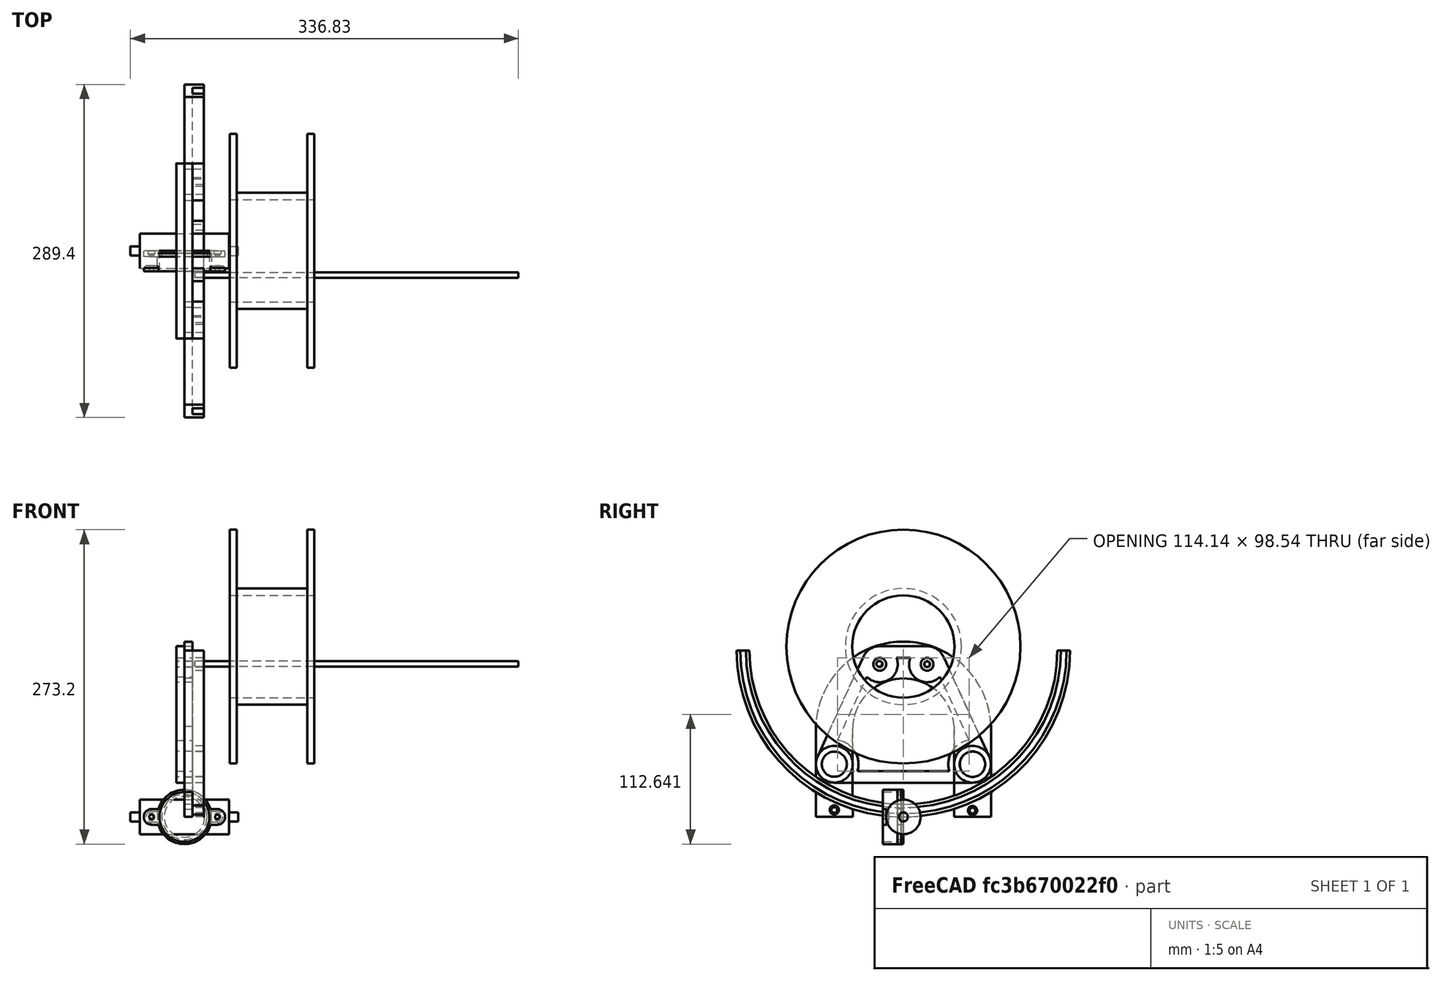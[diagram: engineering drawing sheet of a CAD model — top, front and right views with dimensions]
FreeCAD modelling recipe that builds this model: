
FCSTD DOCUMENT  (FreeCAD 1.1R39057 (Git))
Label: filament dryer new version
License: All rights reserved
objects: App::Link×17, App::FeaturePython×14, Sketcher::SketchObject×9, PartDesign::Pad×8, PartDesign::Body×7, PartDesign::Revolution×2, PartDesign::Chamfer×1, PartDesign::Hole×1, PartDesign::Fillet×1, PartDesign::SubShapeBinder×1, Assembly::JointGroup×1, Assembly::AssemblyObject×1
note: 65 computed .brp shape members not serialized (recipe doc carries the construction recipe); baked Part::Feature solids carry a one-line shape summary decoded from their .brp

FEATURE [Sketcher::SketchObject] Sketch
  ArcFitTolerance = 1e-06
  AttachmentSupport = -> [XZ_Plane]
  FullyConstrained = false
  MakeInternals = false
  MapMode = 5
  Placement = pos=(0,0,0) rot=(1,0,0;1.5708rad)
  sketch-geometry (8):
    g0: LineSegment StartX=-36.586 StartY=44.45 StartZ=0 EndX=36.586 EndY=44.45 EndZ=0
    g1: LineSegment StartX=-36.586 StartY=44.45 StartZ=0 EndX=-36.586 EndY=101.6 EndZ=0
    g2: LineSegment StartX=36.586 StartY=44.45 StartZ=0 EndX=36.586 EndY=101.6 EndZ=0
    g3: LineSegment StartX=-36.586 StartY=101.6 StartZ=0 EndX=-30.586 EndY=101.6 EndZ=0
    g4: LineSegment StartX=-30.586 StartY=101.6 StartZ=0 EndX=-30.586 EndY=50.45 EndZ=0
    g5: LineSegment StartX=30.586 StartY=101.6 StartZ=0 EndX=30.586 EndY=50.45 EndZ=0
    g6: LineSegment StartX=30.586 StartY=101.6 StartZ=0 EndX=36.586 EndY=101.6 EndZ=0
    g7: LineSegment StartX=-30.586 StartY=50.45 StartZ=0 EndX=30.586 EndY=50.45 EndZ=0
  constraints (21):
    c: Distance(g0) = 73.172
    c: Distance(g-1,g0) = 44.45
    c: Symmetric(g0,g0,g-2)
    c: Coincident(g1,g0)
    c: Vertical(g1)
    c: Coincident(g2,g0)
    c: Vertical(g2)
    c: Distance(g1,g-1) = 101.6
    c: Coincident(g3,g1)
    c: Coincident(g6,g2)
    c: Horizontal(g3)
    c: Vertical(g4)
    c: Vertical(g5)
    c: Symmetric(g5,g4,g-2)
    c: Distance(g1,g4) = 6
    c: Coincident(g3,g4)
    c: PointOnObject(g6,g5)
    c: Horizontal(g7)
    c: Distance(g0,g7) = 6
    c: Coincident(g4,g7)
    c: Coincident(g5,g7)
FEATURE [PartDesign::Revolution] Revolution
  Angle = 360
  Angle2 = 60
  Axis = (1,0,0)
  Base = (0,0,0)
  Placement = pos=(0,0,0) rot=(1,0,0;1.5708rad)
  Profile = -> Sketch
  ReferenceAxis = -> X_Axis
  Refine = true
  Reversed = true
  Suppressed = false
  Type = 0
FEATURE [PartDesign::Body] Body  label="spool filament"
  AllowCompound = false
  Group = -> [Sketch,Revolution]
  Origin = -> Origin
  Placement = pos=(76,0,148) rot=(0,0,1;0rad)
  Tip = -> Revolution
FEATURE [Sketcher::SketchObject] Sketch001
  ArcFitTolerance = 1e-06
  AttachmentSupport = -> [YZ_Plane001]
  FullyConstrained = false
  MakeInternals = false
  MapMode = 5
  Placement = pos=(0,0,0) rot=(0.57735,0.57735,0.57735;2.0944rad)
  expr: Constraints[3] = 133.7 * 2 mm
  sketch-geometry (31):
    g0: Circle CenterX=-60 CenterY=45.7733 CenterZ=0 NormalX=0 NormalY=0 NormalZ=1 AngleXU=0 Radius=11.075
    g1: Circle CenterX=60 CenterY=45.7733 CenterZ=0 NormalX=0 NormalY=0 NormalZ=1 AngleXU=0 Radius=11.075
    g2: ArcOfCircle CenterX=0 CenterY=144.7 CenterZ=0 NormalX=0 NormalY=0 NormalZ=1 AngleXU=0 Radius=133.7 StartAngle=3.14159 EndAngle=4.10707
    g3: LineSegment [constr] StartX=-133.7 StartY=144.7 StartZ=0 EndX=133.7 EndY=144.7 EndZ=0
    g4: LineSegment [constr] StartX=-133.7 StartY=144.7 StartZ=0 EndX=133.7 EndY=144.7 EndZ=0
    g5: ArcOfCircle CenterX=0 CenterY=144.7 CenterZ=0 NormalX=0 NormalY=0 NormalZ=1 AngleXU=0 Radius=144.7 StartAngle=3.14159 EndAngle=4.15941
    g6: LineSegment StartX=-133.7 StartY=144.7 StartZ=0 EndX=-144.7 EndY=144.7 EndZ=0
    g7: LineSegment StartX=133.7 StartY=144.7 StartZ=0 EndX=144.7 EndY=144.7 EndZ=0
    g8: LineSegment StartX=-76.0782 StartY=46.2231 StartZ=0 EndX=-76.0782 EndY=34.7555 EndZ=0
    g9: LineSegment StartX=76.0296 StartY=48.9403 StartZ=0 EndX=76.0296 EndY=34.7219 EndZ=0
    g10: LineSegment StartX=-76 StartY=21.5656 StartZ=0 EndX=-76 EndY=0 EndZ=0
    g11: LineSegment StartX=76 StartY=21.5656 StartZ=0 EndX=76 EndY=0 EndZ=0
    g12: LineSegment StartX=-44.0838 StartY=46.2231 StartZ=0 EndX=-44.0838 EndY=18.4768 EndZ=0
    g13: LineSegment StartX=44 StartY=48.9403 StartZ=0 EndX=44 EndY=18.4475 EndZ=0
    g14: LineSegment StartX=-44 StartY=6.85193 StartZ=0 EndX=-44 EndY=0 EndZ=0
    g15: LineSegment StartX=43.9992 StartY=6.85167 StartZ=0 EndX=43.9992 EndY=0 EndZ=0
    g16: LineSegment StartX=-76 StartY=0 StartZ=0 EndX=-44 EndY=0 EndZ=0
    g17: LineSegment StartX=43.9992 StartY=0 StartZ=0 EndX=76 EndY=0 EndZ=0
    g18: ArcOfCircle CenterX=0 CenterY=144.7 CenterZ=0 NormalX=0 NormalY=0 NormalZ=1 AngleXU=0 Radius=144.7 StartAngle=4.40342 EndAngle=5.02135
    g19: ArcOfCircle CenterX=0 CenterY=144.7 CenterZ=0 NormalX=0 NormalY=0 NormalZ=1 AngleXU=0 Radius=144.7 StartAngle=5.26537 EndAngle=6.28319
    g20: ArcOfCircle CenterX=0 CenterY=144.7 CenterZ=0 NormalX=0 NormalY=0 NormalZ=1 AngleXU=0 Radius=133.7 StartAngle=5.31726 EndAngle=6.28319
    g21: ArcOfCircle CenterX=0 CenterY=144.7 CenterZ=0 NormalX=0 NormalY=0 NormalZ=1 AngleXU=0 Radius=133.7 StartAngle=4.37638 EndAngle=5.04773
    g22: LineSegment [constr] StartX=-76.0782 StartY=46.2231 StartZ=0 EndX=-44.0838 EndY=46.2231 EndZ=0
    g23: LineSegment [constr] StartX=44 StartY=48.9403 StartZ=0 EndX=76.0296 EndY=48.9403 EndZ=0
    g24: LineSegment StartX=-76.0782 StartY=46.2231 StartZ=0 EndX=-76.0782 EndY=76.2231 EndZ=0
    g25: LineSegment StartX=76.0296 StartY=48.9403 StartZ=0 EndX=76.0296 EndY=78.9403 EndZ=0
    g26: LineSegment StartX=44 StartY=48.9403 StartZ=0 EndX=44 EndY=78.9403 EndZ=0
    g27: LineSegment StartX=-44.0838 StartY=46.2231 StartZ=0 EndX=-44.0838 EndY=76.2231 EndZ=0
    g28: LineSegment [constr] StartX=-44.0838 StartY=76.2231 StartZ=0 EndX=0 EndY=76.2231 EndZ=0
    g29: ArcOfCircle CenterX=0 CenterY=76.2231 CenterZ=0 NormalX=0 NormalY=0 NormalZ=1 AngleXU=0 Radius=44.0838 StartAngle=0.061677 EndAngle=3.14159
    g30: ArcOfCircle CenterX=0 CenterY=76.2231 CenterZ=0 NormalX=0 NormalY=0 NormalZ=1 AngleXU=0 Radius=76.0782 StartAngle=0.0357239 EndAngle=3.14159
  constraints (80):
    c: Diameter(g0) = 22.15
    c: Equal(g1,g0)
    c: Symmetric(g0,g1,g-2)
    c: Diameter(g2) = 267.4
    c: PointOnObject(g2,g-2)
    c: Horizontal(g3)
    c: PointOnObject(g2,g3)
    c: Coincident(g4,g3)
    c: Coincident(g4,g3)
    c: Coincident(g20,g3)
    c: Coincident(g2,g3)
    c: Distance(g2,g-1) = 11
    c: Coincident(g5,g2)
    c: PointOnObject(g-1,g18)
    c: Coincident(g6,g2)
    c: Horizontal(g6)
    c: Coincident(g7,g20)
    c: Horizontal(g7)
    c: Coincident(g19,g7)
    c: Coincident(g5,g6)
    c: PointOnObject(g10,g-1)
    c: Vertical(g8)
    c: PointOnObject(g11,g-1)
    c: Vertical(g9)
    c: Distance(g0,g-2) = 60
    c: PointOnObject(g9,g20)
    c: PointOnObject(g11,g19)
    c: PointOnObject(g14,g-1)
    c: Vertical(g12)
    c: PointOnObject(g15,g-1)
    c: Vertical(g13)
    c: PointOnObject(g12,g21)
    c: PointOnObject(g14,g18)
    c: Coincident(g16,g10)
    c: Coincident(g16,g14)
    c: Coincident(g17,g15)
    c: Coincident(g17,g11)
    c: Equal(g5,g18)
    c: Coincident(g5,g10)
    c: PointOnObject(g18,g14)
    c: Coincident(g5,g18)
    c: Equal(g18,g19)
    c: Coincident(g18,g15)
    c: PointOnObject(g19,g11)
    c: Coincident(g18,g19)
    c: Equal(g2,g20)
    c: Coincident(g21,g13)
    c: PointOnObject(g20,g9)
    c: Coincident(g2,g20)
    c: Equal(g2,g21)
    c: Coincident(g2,g8)
    c: PointOnObject(g21,g12)
    c: Coincident(g2,g21)
    c: Coincident(g22,g8)
    c: Coincident(g22,g12)
    c: Horizontal(g22)
    c: Coincident(g23,g13)
    c: Coincident(g23,g9)
    c: Horizontal(g23)
    c: Distance(g24) = 30
    c: Coincident(g24,g8)
    c: Vertical(g24)
    c: Coincident(g25,g9)
    c: Vertical(g25)
    c: Coincident(g26,g13)
    c: Vertical(g26)
    c: Coincident(g27,g12)
    c: Vertical(g27)
    c: Equal(g24,g27)
    c: Equal(g27,g26)
    c: Equal(g26,g25)
    c: Coincident(g28,g27)
    c: PointOnObject(g28,g-2)
    c: Horizontal(g28)
    c: Coincident(g29,g28)
    c: Coincident(g29,g27)
    c: Coincident(g29,g26)
    c: Coincident(g30,g28)
    c: Coincident(g30,g24)
    c: Coincident(g30,g25)
FEATURE [PartDesign::Pad] Pad
  Direction = (1,0,0)
  Length = 7
  Length2 = 10
  Placement = pos=(0,0,0) rot=(1,1,1;2.0944rad)
  Profile = -> Sketch001
  ReferenceAxis = -> Sketch001 [N_Axis]
  Refine = true
  Suppressed = false
  Type = 0
FEATURE [Sketcher::SketchObject] Sketch002
  ArcFitTolerance = 1e-06
  AttachmentSupport = -> [Pad]
  ExternalGeometry = -> [Pad]
  FullyConstrained = false
  MakeInternals = false
  MapMode = 5
  Placement = pos=(7,0,0) rot=(0.57735,0.57735,0.57735;2.0944rad)
  sketch-geometry (24):
    g0: ArcOfCircle CenterX=2.39e-14 CenterY=144.7 CenterZ=0 NormalX=0 NormalY=0 NormalZ=1 AngleXU=0 Radius=133.7 StartAngle=3.14159 EndAngle=6.28319
    g1: ArcOfCircle CenterX=2.39e-14 CenterY=144.7 CenterZ=0 NormalX=0 NormalY=0 NormalZ=1 AngleXU=0 Radius=144.7 StartAngle=3.14159 EndAngle=6.28319
    g2: ArcOfCircle CenterX=2.39e-14 CenterY=144.7 CenterZ=0 NormalX=0 NormalY=0 NormalZ=1 AngleXU=0 Radius=141.7 StartAngle=3.14159 EndAngle=6.28319
    g3: ArcOfCircle CenterX=2.39e-14 CenterY=144.7 CenterZ=0 NormalX=0 NormalY=0 NormalZ=1 AngleXU=0 Radius=136.7 StartAngle=3.14159 EndAngle=6.28319
    g4: LineSegment StartX=133.7 StartY=144.7 StartZ=0 EndX=136.7 EndY=144.7 EndZ=0
    g5: LineSegment StartX=141.7 StartY=144.7 StartZ=0 EndX=144.7 EndY=144.7 EndZ=0
    g6: LineSegment StartX=-136.7 StartY=144.7 StartZ=0 EndX=-133.7 EndY=144.7 EndZ=0
    g7: LineSegment StartX=-144.7 StartY=144.7 StartZ=0 EndX=-141.7 EndY=144.7 EndZ=0
    g8: Circle CenterX=-60 CenterY=6 CenterZ=0 NormalX=0 NormalY=0 NormalZ=1 AngleXU=0 Radius=2.5
    g9: Circle CenterX=-60 CenterY=6 CenterZ=0 NormalX=0 NormalY=0 NormalZ=1 AngleXU=0 Radius=4
    g10: LineSegment [constr] StartX=-60 StartY=10.7501 StartZ=0 EndX=-60 EndY=-7.18174 EndZ=0
    g11: Circle CenterX=60 CenterY=5.5 CenterZ=0 NormalX=0 NormalY=0 NormalZ=1 AngleXU=0 Radius=2.5
    g12: Circle CenterX=60 CenterY=5.5 CenterZ=0 NormalX=0 NormalY=0 NormalZ=1 AngleXU=0 Radius=4
    g13: Circle CenterX=-60 CenterY=45.7733 CenterZ=0 NormalX=0 NormalY=0 NormalZ=1 AngleXU=0 Radius=10.901
    g14: Circle CenterX=-60 CenterY=45.7733 CenterZ=0 NormalX=0 NormalY=0 NormalZ=1 AngleXU=0 Radius=16
    g15: Circle CenterX=59.9992 CenterY=45.7733 CenterZ=0 NormalX=0 NormalY=0 NormalZ=1 AngleXU=0 Radius=16
    g16: Circle CenterX=59.9992 CenterY=45.7733 CenterZ=0 NormalX=0 NormalY=0 NormalZ=1 AngleXU=0 Radius=11.0656
    g17: LineSegment [constr] StartX=0 StartY=152.301 StartZ=0 EndX=0 EndY=120.307 EndZ=0
    g18: LineSegment [constr] StartX=0 StartY=136.304 StartZ=0 EndX=37.5871 EndY=136.304 EndZ=0
    g19: Circle CenterX=-20.575 CenterY=132.671 CenterZ=0 NormalX=0 NormalY=0 NormalZ=1 AngleXU=0 Radius=2.575
    g20: Circle CenterX=-20.575 CenterY=132.671 CenterZ=0 NormalX=0 NormalY=0 NormalZ=1 AngleXU=0 Radius=5.575
    g21: ArcOfCircle [constr] CenterX=8.5e-15 CenterY=76.2231 CenterZ=0 NormalX=0 NormalY=0 NormalZ=1 AngleXU=0 Radius=60.081 StartAngle=0.738747 EndAngle=2.47765
    g22: Circle CenterX=20.575 CenterY=132.671 CenterZ=0 NormalX=0 NormalY=0 NormalZ=1 AngleXU=0 Radius=5.575
    g23: Circle CenterX=20.575 CenterY=132.671 CenterZ=0 NormalX=0 NormalY=0 NormalZ=1 AngleXU=0 Radius=2.575
  constraints (50):
    c: Coincident(g0,g-5)
    c: Coincident(g0,g-3)
    c: Coincident(g0,g-4)
    c: Coincident(g1,g0)
    c: Coincident(g1,g-3)
    c: Coincident(g1,g-4)
    c: Coincident(g2,g0)
    c: PointOnObject(g2,g-3)
    c: PointOnObject(g2,g-4)
    c: Coincident(g3,g0)
    c: PointOnObject(g3,g-3)
    c: PointOnObject(g3,g-4)
    c: Distance(g2,g1) = 3
    c: Distance(g3,g0) = 3
    c: Coincident(g4,g0)
    c: Coincident(g4,g3)
    c: Coincident(g5,g2)
    c: Coincident(g5,g1)
    c: Coincident(g6,g3)
    c: Coincident(g6,g0)
    c: Coincident(g7,g1)
    c: Coincident(g7,g2)
    c: Coincident(g9,g8)
    c: Diameter(g8) = 5
    c: Distance(g9,g-1) = 2
    c: Symmetric(g-7,g-6,g10)
    c: PointOnObject(g8,g10)
    c: Coincident(g12,g11)
    c: Diameter(g11) = 5
    c: Diameter(g12) = 8
    c: Tangent(g13,g-8) = -1.5708
    c: Coincident(g14,g13)
    c: Coincident(g16,g15)
    c: PointOnObject(g17,g-2)
    c: PointOnObject(g17,g-2)
    c: PointOnObject(g17,g-10)
    c: PointOnObject(g17,g-11)
    c: Symmetric(g17,g17,g18)
    c: PointOnObject(g18,g17)
    c: Diameter(g19) = 5.15
    c: Coincident(g20,g19)
    c: Distance(g20,g19) = 3
    c: Coincident(g21,g-11)
    c: PointOnObject(g18,g21)
    c: PointOnObject(g19,g21)
    c: Distance(g20,g17) = 15
    c: Diameter(g23) = 5.15
    c: Coincident(g22,g23)
    c: Distance(g22,g23) = 3
    c: Equal(g9,g12)
FEATURE [PartDesign::Pad] Pad001
  BaseFeature = -> Pad
  Direction = (1,0,0)
  Length = 10
  Length2 = 10
  Placement = pos=(0,0,0) rot=(1,1,1;2.0944rad)
  Profile = -> Sketch002
  ReferenceAxis = -> Sketch002 [N_Axis]
  Refine = true
  Suppressed = false
  Type = 0
FEATURE [PartDesign::Body] Body001  label="spool holder"
  AllowCompound = false
  Group = -> [Sketch001,Pad,Sketch002,Pad001]
  Origin = -> Origin001
  Tip = -> Pad001
FEATURE [Sketcher::SketchObject] Sketch003
  ArcFitTolerance = 1e-06
  AttachmentSupport = -> [YZ_Plane002]
  FullyConstrained = false
  MakeInternals = false
  MapMode = 5
  Placement = pos=(0,0,0) rot=(0.57735,0.57735,0.57735;2.0944rad)
  sketch-geometry (2):
    g0: Circle [constr] CenterX=0 CenterY=0 CenterZ=0 NormalX=0 NormalY=0 NormalZ=1 AngleXU=0 Radius=0
    g1: Circle CenterX=0 CenterY=0 CenterZ=0 NormalX=0 NormalY=0 NormalZ=1 AngleXU=0 Radius=2.5
  constraints (2):
    c: Coincident(g1,g0)
    c: Diameter(g1) = 5
FEATURE [PartDesign::Pad] Pad002
  Direction = (1,0,0)
  Length = 281
  Length2 = 10
  Placement = pos=(0,0,0) rot=(1,1,1;2.0944rad)
  Profile = -> Sketch003
  ReferenceAxis = -> Sketch003 [N_Axis]
  Refine = true
  Suppressed = false
  Type = 0
FEATURE [PartDesign::Body] Body002  label="spoon holder joins"
  AllowCompound = false
  Group = -> [Sketch003,Pad002]
  Origin = -> Origin002
  Placement = pos=(9,-21,133) rot=(0,0,1;0rad)
  Tip = -> Pad002
FEATURE [Sketcher::SketchObject] Sketch004
  ArcFitTolerance = 1e-06
  AttachmentSupport = -> [XZ_Plane003]
  FullyConstrained = true
  MakeInternals = false
  MapMode = 5
  Placement = pos=(0,0,0) rot=(1,0,0;1.5708rad)
  expr: Constraints[17] = 3.925 mm
  sketch-geometry (8):
    g0: LineSegment StartX=-46.8333 StartY=0 StartZ=0 EndX=-46.8333 EndY=3.925 EndZ=0
    g1: LineSegment StartX=-46.8333 StartY=3.925 StartZ=0 EndX=-38.8333 EndY=3.925 EndZ=0
    g2: LineSegment StartX=-38.8333 StartY=3.925 StartZ=0 EndX=-38.8333 EndY=15 EndZ=0
    g3: LineSegment StartX=-38.8333 StartY=15 StartZ=0 EndX=38.8333 EndY=15 EndZ=0
    g4: LineSegment StartX=38.8333 StartY=15 StartZ=0 EndX=38.8333 EndY=3.925 EndZ=0
    g5: LineSegment StartX=38.8333 StartY=3.925 StartZ=0 EndX=46.8333 EndY=3.925 EndZ=0
    g6: LineSegment StartX=46.8333 StartY=3.925 StartZ=0 EndX=46.8333 EndY=1.2372e-12 EndZ=0
    g7: LineSegment StartX=-46.8333 StartY=0 StartZ=0 EndX=46.8333 EndY=1.2372e-12 EndZ=0
  constraints (23):
    c: PointOnObject(g0,g-1)
    c: Vertical(g0)
    c: Coincident(g1,g0)
    c: Horizontal(g1)
    c: Coincident(g2,g1)
    c: Vertical(g2)
    c: Coincident(g3,g2)
    c: Coincident(g4,g3)
    c: Coincident(g5,g4)
    c: Horizontal(g5)
    c: Vertical(g6)
    c: Vertical(g4)
    c: Equal(g2,g4)
    c: Equal(g0,g6)
    c: Symmetric(g2,g3,g-2)
    c: Coincident(g6,g5)
    c: DistanceX(g1,g1) = 8
    c: DistanceY(g0,g0) = 3.925
    c: Distance(g2,g-1) = 15
    c: Coincident(g7,g0)
    c: Coincident(g7,g6)
    c: DistanceX(g7,g7) = 93.6666
    c: Equal(g1,g5)
FEATURE [PartDesign::Revolution] Revolution001
  Angle = 360
  Angle2 = 60
  Axis = (1,0,0)
  Base = (0,0,0)
  Placement = pos=(0,0,0) rot=(1,0,0;1.5708rad)
  Profile = -> Sketch004
  ReferenceAxis = -> X_Axis003
  Refine = true
  Suppressed = false
  Type = 0
FEATURE [PartDesign::Body] Body003  label="side bearing cilinders"
  AllowCompound = false
  Group = -> [Sketch004,Revolution001]
  Origin = -> Origin003
  Tip = -> Revolution001
FEATURE [Sketcher::SketchObject] Sketch006
  ArcFitTolerance = 1e-06
  AttachmentSupport = -> [XZ_Plane006]
  FullyConstrained = true
  MakeInternals = false
  MapMode = 5
  Placement = pos=(0,0,0) rot=(1,0,0;1.5708rad)
  sketch-geometry (3):
    g0: Circle CenterX=0 CenterY=0 CenterZ=0 NormalX=0 NormalY=0 NormalZ=1 AngleXU=0 Radius=23.6
    g1: Circle CenterX=0 CenterY=0 CenterZ=0 NormalX=0 NormalY=0 NormalZ=1 AngleXU=0 Radius=17.6
    g2: Circle CenterX=0 CenterY=0 CenterZ=0 NormalX=0 NormalY=0 NormalZ=1 AngleXU=0 Radius=21.6
  constraints (6):
    c: Diameter(g0) = 47.2
    c: Coincident(g0,g-1)
    c: Coincident(g1,g0)
    c: Distance(g1,g0) = 6
    c: Coincident(g2,g0)
    c: Distance(g2,g0) = 2
FEATURE [PartDesign::Pad] Pad004
  Direction = (0,-1,2e-16)
  Length = 17.8
  Length2 = 10
  Placement = pos=(0,0,0) rot=(1,0,0;1.5708rad)
  Profile = -> Sketch006 [Edge1,Edge3]
  ReferenceAxis = -> Sketch006 [N_Axis]
  Refine = true
  Suppressed = false
  Type = 0
FEATURE [PartDesign::Pad] Pad005
  BaseFeature = -> Pad004
  Direction = (0,-1,2e-16)
  Length = 2
  Length2 = 10
  Placement = pos=(0,0,0) rot=(1,0,0;1.5708rad)
  Profile = -> Sketch006 [Edge3,Edge2]
  ReferenceAxis = -> Sketch006 [N_Axis]
  Refine = true
  Suppressed = false
  Type = 0
FEATURE [Sketcher::SketchObject] Sketch007
  ArcFitTolerance = 1e-06
  AttachmentSupport = -> [Pad005]
  ExternalGeometry = -> [Pad005]
  FullyConstrained = true
  MakeInternals = false
  MapMode = 5
  Placement = pos=(0,-17.8,0) rot=(1,0,0;1.5708rad)
  sketch-geometry (10):
    g0: ArcOfCircle CenterX=0 CenterY=0 CenterZ=0 NormalX=0 NormalY=0 NormalZ=1 AngleXU=0 Radius=23.6 StartAngle=2.8518 EndAngle=3.43139
    g1: ArcOfCircle CenterX=-28.6 CenterY=0 CenterZ=0 NormalX=0 NormalY=0 NormalZ=1 AngleXU=0 Radius=6.74389 StartAngle=1.5708 EndAngle=4.71239
    g2: ArcOfCircle CenterX=28.6 CenterY=0 CenterZ=0 NormalX=0 NormalY=0 NormalZ=1 AngleXU=0 Radius=6.74389 StartAngle=4.71239 EndAngle=7.85398
    g3: LineSegment StartX=-28.6 StartY=6.74389 StartZ=0 EndX=-22.6159 EndY=6.74389 EndZ=0
    g4: LineSegment StartX=-28.6 StartY=-6.74389 StartZ=0 EndX=-22.6159 EndY=-6.74389 EndZ=0
    g5: LineSegment StartX=22.6159 StartY=6.74389 StartZ=0 EndX=28.6 EndY=6.74389 EndZ=0
    g6: LineSegment StartX=22.6159 StartY=-6.74389 StartZ=0 EndX=28.6 EndY=-6.74389 EndZ=0
    g7: Circle CenterX=-28.6 CenterY=0 CenterZ=0 NormalX=0 NormalY=0 NormalZ=1 AngleXU=0 Radius=1.95
    g8: Circle CenterX=28.6 CenterY=0 CenterZ=0 NormalX=0 NormalY=0 NormalZ=1 AngleXU=0 Radius=1.95
    g9: ArcOfCircle CenterX=0 CenterY=0 CenterZ=0 NormalX=0 NormalY=0 NormalZ=1 AngleXU=0 Radius=23.6 StartAngle=5.99339 EndAngle=6.57298
  constraints (28):
    c: Coincident(g0,g-1)
    c: Tangent(g0,g-3)
    c: PointOnObject(g1,g-1)
    c: Equal(g2,g1)
    c: Symmetric(g1,g2,g-2)
    c: Distance(g1,g0) = 5
    c: Coincident(g2,g5) = 1.5708
    c: Coincident(g2,g6) = -1.5708
    c: Block(g1)
    c: Block(g2)
    c: Coincident(g3,g1)
    c: Coincident(g4,g1)
    c: PointOnObject(g6,g9)
    c: Diameter(g7) = 3.9
    c: Coincident(g7,g1)
    c: Diameter(g8) = 3.9
    c: Coincident(g8,g2)
    c: Coincident(g9,g5)
    c: Coincident(g0,g3)
    c: Equal(g0,g9)
    c: Coincident(g0,g4)
    c: PointOnObject(g9,g6)
    c: Coincident(g0,g9)
    c: Horizontal(g4)
    c: Horizontal(g3)
    c: Horizontal(g5)
    c: Horizontal(g6)
    c: DistanceY(g1,g1) = 6.74389
FEATURE [PartDesign::Pad] Pad006
  BaseFeature = -> Pad005
  Direction = (0,-1,2e-16)
  Length = 5
  Length2 = 10
  Placement = pos=(0,0,0) rot=(1,0,0;1.5708rad)
  Profile = -> Sketch007
  ReferenceAxis = -> Sketch007 [N_Axis]
  Refine = true
  Reversed = true
  Suppressed = false
  Type = 0
FEATURE [PartDesign::Chamfer] Chamfer
  Angle = 45
  Base = -> Pad006 [Edge5,Edge26,Edge27,Edge25,Edge18,Edge17,Edge19]
  BaseFeature = -> Pad006
  ChamferType = 0
  FlipDirection = false
  Placement = pos=(0,0,0) rot=(1,0,0;1.5708rad)
  Refine = true
  Size = 2
  Size2 = 1
  SupportTransform = false
  Suppressed = false
  UseAllEdges = false
FEATURE [PartDesign::Body] Body005  label=" thermal and humidity sensor case 1"
  AllowCompound = false
  Group = -> [Sketch006,Pad004,Pad005,Sketch007,Pad006,Chamfer]
  Origin = -> Origin006
  Tip = -> Chamfer
FEATURE [Sketcher::SketchObject] Sketch008
  ArcFitTolerance = 1e-06
  AttachmentSupport = -> [XZ_Plane007]
  FullyConstrained = false
  MakeInternals = false
  MapMode = 5
  Placement = pos=(0,0,0) rot=(1,0,0;1.5708rad)
  expr: Constraints[7] = 6.74 * 2 mm
  sketch-geometry (11):
    g0: ArcOfCircle CenterX=0 CenterY=0 CenterZ=0 NormalX=0 NormalY=0 NormalZ=1 AngleXU=0 Radius=23.6 StartAngle=3.43122 EndAngle=5.99356
    g1: Circle CenterX=0 CenterY=0 CenterZ=0 NormalX=0 NormalY=0 NormalZ=1 AngleXU=0 Radius=19.6
    g2: ArcOfCircle CenterX=-28.6 CenterY=0 CenterZ=0 NormalX=0 NormalY=0 NormalZ=1 AngleXU=0 Radius=6.74 StartAngle=1.5708 EndAngle=4.71238
    g3: ArcOfCircle CenterX=28.6 CenterY=0 CenterZ=0 NormalX=0 NormalY=0 NormalZ=1 AngleXU=0 Radius=6.74 StartAngle=4.71239 EndAngle=7.85398
    g4: LineSegment StartX=-28.6 StartY=6.74 StartZ=0 EndX=-22.6171 EndY=6.74 EndZ=0
    g5: LineSegment StartX=-28.6 StartY=-6.74 StartZ=0 EndX=-22.6171 EndY=-6.74 EndZ=0
    g6: LineSegment StartX=22.6171 StartY=6.74 StartZ=0 EndX=28.6 EndY=6.74 EndZ=0
    g7: LineSegment StartX=22.6171 StartY=-6.74 StartZ=0 EndX=28.6 EndY=-6.74 EndZ=0
    g8: ArcOfCircle CenterX=0 CenterY=0 CenterZ=0 NormalX=0 NormalY=0 NormalZ=1 AngleXU=0 Radius=23.6 StartAngle=0.289625 EndAngle=2.85197
    g9: Circle CenterX=-28.6 CenterY=0 CenterZ=0 NormalX=0 NormalY=0 NormalZ=1 AngleXU=0 Radius=2.11661
    g10: Circle CenterX=28.6 CenterY=0 CenterZ=0 NormalX=0 NormalY=0 NormalZ=1 AngleXU=0 Radius=2.11661
  constraints (25):
    c: Diameter(g0) = 47.2
    c: Coincident(g0,g-1)
    c: Coincident(g1,g0)
    c: Distance(g1,g0) = 4
    c: PointOnObject(g2,g-1)
    c: Equal(g3,g2)
    c: Symmetric(g2,g3,g-2)
    c: Diameter(g2) = 13.48
    c: Distance(g3,g0) = 5
    c: Horizontal(g5)
    c: Coincident(g2,g4)
    c: Coincident(g3,g6) = 1.5708
    c: Coincident(g3,g7) = -1.5708
    c: Vertical(g2,g2)
    c: Coincident(g2,g5)
    c: PointOnObject(g6,g8)
    c: Coincident(g8,g4)
    c: Coincident(g0,g5)
    c: Equal(g0,g8)
    c: Coincident(g0,g7)
    c: PointOnObject(g8,g6)
    c: Coincident(g0,g8)
    c: Coincident(g9,g2)
    c: Coincident(g10,g3)
    c: Equal(g10,g9)
FEATURE [PartDesign::Pad] Pad007
  Direction = (0,-1,2e-16)
  Length = 5
  Length2 = 10
  Placement = pos=(0,0,0) rot=(1,0,0;1.5708rad)
  Profile = -> Sketch008 [Edge5,Edge4,Edge3,Edge9,Edge2,Edge1,Edge8,Edge7,Edge6]
  ReferenceAxis = -> Sketch008 [N_Axis]
  Refine = true
  Suppressed = false
  Type = 0
FEATURE [PartDesign::Hole] Hole
  BaseFeature = -> Pad007
  CustomThreadClearance = 0
  Depth = 171.97
  DepthType = 1
  Diameter = 3.9
  DrillForDepth = false
  DrillPoint = 1
  DrillPointAngle = 118
  HoleCutCountersinkAngle = 90
  HoleCutCustomValues = false
  HoleCutDepth = 2.5
  HoleCutDiameter = 6.1
  HoleCutType = 3
  ModelThread = false
  Placement = pos=(0,0,0) rot=(1,0,0;1.5708rad)
  Profile = -> Sketch008 [Edge10,Edge11]
  Refine = true
  Reversed = true
  Suppressed = false
  Tapered = false
  TaperedAngle = 90
  ThreadClass = 0
  ThreadDepth = 171.97
  ThreadDepthType = 0
  ThreadDirection = 0
  ThreadFit = 0
  ThreadSize = 0
  ThreadType = 0
  Threaded = false
  UseCustomThreadClearance = false
FEATURE [PartDesign::Fillet] Fillet
  Base = -> Hole [Edge13,Edge15,Edge14,Edge12,Edge9,Edge3,Edge6,Edge11,Edge17]
  BaseFeature = -> Hole
  Placement = pos=(0,0,0) rot=(1,0,0;1.5708rad)
  Radius = 1
  Refine = true
  SupportTransform = false
  Suppressed = false
  UseAllEdges = false
FEATURE [PartDesign::Body] Body006  label="thermal and humidity sensor case 2"
  AllowCompound = false
  Group = -> [Sketch008,Pad007,Hole,Fillet]
  Origin = -> Origin007
  Tip = -> Fillet
FEATURE [PartDesign::SubShapeBinder] Binder
  BindCopyOnChange = 0
  BindMode = 0
  ClaimChildren = false
  Context = -> Body004 [Binder.]
  Fuse = false
  MakeFace = true
  OffsetFill = false
  OffsetIntersection = false
  OffsetJoinType = 0
  OffsetOpenResult = false
  PartialLoad = false
  Refine = true
  Relative = true
  Support = -> [Body001[Pad001.Face33,Pad001.Face34]]
  _Version = 2
FEATURE [Sketcher::SketchObject] Sketch005
  ArcFitTolerance = 1e-06
  AttachmentSupport = -> [YZ_Plane004]
  ExternalGeometry = -> [Binder]
  FullyConstrained = false
  MakeInternals = false
  MapMode = 5
  Placement = pos=(0,0,0) rot=(0.57735,0.57735,0.57735;2.0944rad)
  sketch-geometry (24):
    g0: Circle CenterX=-60 CenterY=45.77 CenterZ=0 NormalX=0 NormalY=0 NormalZ=1 AngleXU=0 Radius=11
    g1: Circle CenterX=59.9999 CenterY=45.77 CenterZ=0 NormalX=0 NormalY=0 NormalZ=1 AngleXU=0 Radius=11
    g2: LineSegment [constr] StartX=-60 StartY=45.77 StartZ=0 EndX=-60 EndY=0 EndZ=0
    g3: ArcOfCircle CenterX=-60 CenterY=45.77 CenterZ=0 NormalX=0 NormalY=0 NormalZ=1 AngleXU=0 Radius=16 StartAngle=2.71191 EndAngle=4.71239
    g4: ArcOfCircle CenterX=59.9999 CenterY=45.77 CenterZ=0 NormalX=0 NormalY=0 NormalZ=1 AngleXU=0 Radius=16 StartAngle=4.71239 EndAngle=6.71287
    g5: LineSegment StartX=-39.8754 StartY=39.77 StartZ=0 EndX=39.8753 EndY=39.77 EndZ=0
    g6: ArcOfCircle CenterX=59.9999 CenterY=45.77 CenterZ=0 NormalX=0 NormalY=0 NormalZ=1 AngleXU=0 Radius=21 StartAngle=1.71073 EndAngle=3.43134
    g7: ArcOfCircle CenterX=-60 CenterY=45.77 CenterZ=0 NormalX=0 NormalY=0 NormalZ=1 AngleXU=0 Radius=21 StartAngle=5.99343 EndAngle=7.71405
    g8: GeomPoint [constr] X=0 Y=151.304 Z=0
    g9: Circle CenterX=-20.575 CenterY=132.671 CenterZ=0 NormalX=0 NormalY=0 NormalZ=1 AngleXU=0 Radius=2.575
    g10: Circle CenterX=20.575 CenterY=132.671 CenterZ=0 NormalX=0 NormalY=0 NormalZ=1 AngleXU=0 Radius=2.36628
    g11: Circle [constr] CenterX=-20.575 CenterY=132.671 CenterZ=0 NormalX=0 NormalY=0 NormalZ=1 AngleXU=0 Radius=5.63976
    g12: Circle [constr] CenterX=20.575 CenterY=132.671 CenterZ=0 NormalX=0 NormalY=0 NormalZ=1 AngleXU=0 Radius=5.575
    g13: LineSegment StartX=-74.5456 StartY=52.4353 StartZ=0 EndX=-34.7931 EndY=139.186 EndZ=0
    g14: LineSegment StartX=74.5455 StartY=52.4353 StartZ=0 EndX=34.7931 EndY=139.186 EndZ=0
    g15: ArcOfCircle CenterX=-20.575 CenterY=132.671 CenterZ=0 NormalX=0 NormalY=0 NormalZ=1 AngleXU=0 Radius=15.6398 StartAngle=3.91379 EndAngle=6.6521
    g16: ArcOfCircle CenterX=20.575 CenterY=132.671 CenterZ=0 NormalX=0 NormalY=0 NormalZ=1 AngleXU=0 Radius=15.6398 StartAngle=0.429681 EndAngle=1.5708
    g17: LineSegment StartX=-57.071 StartY=66.5647 StartZ=0 EndX=-31.779 EndY=121.759 EndZ=0
    g18: LineSegment StartX=57.071 StartY=66.5647 StartZ=0 EndX=31.779 EndY=121.759 EndZ=0
    g19: LineSegment StartX=-5.9875 StartY=138.311 StartZ=0 EndX=5.9875 EndY=138.311 EndZ=0
    g20: ArcOfCircle CenterX=-20.575 CenterY=132.671 CenterZ=0 NormalX=0 NormalY=0 NormalZ=1 AngleXU=0 Radius=15.6398 StartAngle=1.5708 EndAngle=2.71191
    g21: ArcOfCircle CenterX=20.575 CenterY=132.671 CenterZ=0 NormalX=0 NormalY=0 NormalZ=1 AngleXU=0 Radius=15.6398 StartAngle=2.77268 EndAngle=5.51099
    g22: LineSegment StartX=-20.575 StartY=148.311 StartZ=0 EndX=20.575 EndY=148.311 EndZ=0
    g23: LineSegment StartX=-60 StartY=29.77 StartZ=0 EndX=59.9999 EndY=29.77 EndZ=0
  constraints (52):
    c: Diameter(g0) = 22
    c: PointOnObject(g2,g-1)
    c: Block(g1)
    c: PointOnObject(g3,g2)
    c: Distance(g0,g3) = 5
    c: Distance(g1,g4) = 5
    c: Block(g2)
    c: Coincident(g0,g2)
    c: Coincident(g3,g0)
    c: Coincident(g4,g1)
    c: Horizontal(g5)
    c: Coincident(g6,g1)
    c: Coincident(g6,g5)
    c: Coincident(g7,g0)
    c: Coincident(g7,g5)
    c: Distance(g0,g7) = 10
    c: Distance(g6,g1) = 10
    c: PointOnObject(g8,g-2)
    c: Coincident(g9,g-5)
    c: Equal(g9,g-5)
    c: Coincident(g10,g-4)
    c: Coincident(g11,g9)
    c: Coincident(g12,g10)
    c: Tangent(g12,g-4)
    c: Coincident(g15,g9)
    c: Coincident(g16,g10)
    c: Distance(g11,g15) = 10
    c: Block(g11)
    c: Tangent(g4,g14) = -1.5708
    c: Tangent(g3,g13) = 1.5708
    c: Coincident(g17,g7)
    c: Coincident(g18,g6)
    c: Parallel(g18,g14)
    c: Parallel(g17,g13)
    c: Distance(g13,g17) = 10
    c: Distance(g14,g18) = 10
    c: Coincident(g20,g13) = 1.5708
    c: Coincident(g15,g17)
    c: Coincident(g21,g18)
    c: Tangent(g16,g14) = -1.5708
    c: PointOnObject(g19,g21)
    c: Coincident(g15,g19)
    c: Coincident(g15,g20)
    c: Equal(g16,g21)
    c: PointOnObject(g21,g19)
    c: Coincident(g16,g21)
    c: Coincident(g22,g20)
    c: Coincident(g22,g16)
    c: Horizontal(g22)
    c: Coincident(g23,g3)
    c: Tangent(g23,g4) = -1.5708
    c: Horizontal(g23)
FEATURE [PartDesign::Pad] Pad008
  Direction = (1,0,0)
  Length = 14
  Length2 = 10
  Midplane = true
  Placement = pos=(0,0,0) rot=(1,1,1;2.0944rad)
  Profile = -> Sketch005
  ReferenceAxis = -> Sketch005 [N_Axis]
  Refine = true
  Suppressed = false
  Type = 0
FEATURE [PartDesign::Body] Body004  label="spoon holder middle section"
  AllowCompound = false
  Group = -> [Sketch005,Binder,Pad008]
  Origin = -> Origin004
  Tip = -> Pad008
FEATURE [App::Link] side_bearing_cilinders  label="side bearing cilinders001"
  LinkPlacement = pos=(53.8333,-60,45.7733) rot=(1,0,0;4.71239rad)
  LinkedObject = -> Body003
  Placement = pos=(53.8333,-60,45.7733) rot=(1,0,0;4.71239rad)
FEATURE [App::Link] side_bearing_cilinders001  label="side bearing cilinders002"
  LinkPlacement = pos=(147.5,-60,45.7733) rot=(-1,0,0;1.5708rad)
  LinkedObject = -> Body003
  Placement = pos=(147.5,-60,45.7733) rot=(-1,0,0;1.5708rad)
FEATURE [App::Link] side_bearing_cilinders002  label="side bearing cilinders003"
  LinkPlacement = pos=(241.167,-60,45.7733) rot=(-1,0,0;1.5708rad)
  LinkedObject = -> Body003
  Placement = pos=(241.167,-60,45.7733) rot=(-1,0,0;1.5708rad)
FEATURE [App::Link] side_bearing_cilinders003  label="side bearing cilinders004"
  LinkPlacement = pos=(147.5,59.9999,45.7733) rot=(-1,0,0;1.5708rad)
  LinkedObject = -> Body003
  Placement = pos=(147.5,59.9999,45.7733) rot=(-1,0,0;1.5708rad)
FEATURE [App::Link] side_bearing_cilinders004  label="side bearing cilinders005"
  LinkPlacement = pos=(53.8333,59.9999,45.7733) rot=(1,0,0;4.71239rad)
  LinkedObject = -> Body003
  Placement = pos=(53.8333,59.9999,45.7733) rot=(1,0,0;4.71239rad)
FEATURE [App::Link] side_bearing_cilinders005  label="side bearing cilinders006"
  LinkPlacement = pos=(241.666,59.9992,45.7733) rot=(1,0,0;1.5708rad)
  LinkedObject = -> Body003
  Placement = pos=(241.666,59.9992,45.7733) rot=(1,0,0;1.5708rad)
FEATURE [App::Link] spoon_holder_middle_section  label="spoon holder middle section001"
  LinkPlacement = pos=(194.333,7.29e-14,0.00330997) rot=(0,0,1;0rad)
  LinkedObject = -> Body004
  Placement = pos=(194.333,7.29e-14,0.00330997) rot=(0,0,1;0rad)
FEATURE [App::Link] spoon_holder_middle_section001  label="spoon holder middle section002"
  LinkPlacement = pos=(100.667,1.3e-15,0.00330997) rot=(0,0,1;0rad)
  LinkedObject = -> Body004
  Placement = pos=(100.667,1.3e-15,0.00330997) rot=(0,0,1;0rad)
FEATURE [App::Link] spool_holder  label="spool holder001"
  LinkedObject = -> Body001
FEATURE [App::FeaturePython] GroundedJoint  # Assembly grounded joint (typed FeaturePython)
  ObjectToGround = -> spool_holder
FEATURE [App::Link] spool_holder001  label="spool holder002"
  LinkPlacement = pos=(292,-0.000813,-2.02853e-06) rot=(0,0,1;3.14159rad)
  LinkedObject = -> Body001
  Placement = pos=(292,-0.000813,-2.02853e-06) rot=(0,0,1;3.14159rad)
FEATURE [App::FeaturePython] Joint  label="Fijo"  # Assembly joint (typed FeaturePython)
  Activated = true
  AngleMax = 0
  AngleMin = 0
  Detach1 = false
  Detach2 = false
  Distance = 0
  Distance2 = 0
  EnableAngleMax = false
  EnableAngleMin = false
  EnableLengthMax = false
  EnableLengthMin = false
  JointType = 0 (Fixed)
  LengthMax = 0
  LengthMin = 0
  Placement1 = pos=(-46.8333,0,7.1e-15) rot=(0.707107,0,0.707107;3.14159rad)
  Placement2 = pos=(7,-60,45.7733) rot=(0.57735,0.57735,0.57735;2.0944rad)
  Reference1 = -> Assembly [side_bearing_cilinders.Edge1,side_bearing_cilinders.Edge1]
  Reference2 = -> Assembly [spool_holder.Edge74,spool_holder.Edge74]
FEATURE [App::FeaturePython] Joint001  label="Fijo001"  # Assembly joint (typed FeaturePython)
  Activated = true
  AngleMax = 0
  AngleMin = 0
  Detach1 = false
  Detach2 = false
  Distance = 0
  Distance2 = 0
  EnableAngleMax = false
  EnableAngleMin = false
  EnableLengthMax = false
  EnableLengthMin = false
  JointType = 0 (Fixed)
  LengthMax = 0
  LengthMin = 0
  Placement1 = pos=(46.8333,0,0) rot=(0.707107,0,0.707107;3.14159rad)
  Placement2 = pos=(-2.84e-14,-60,45.77) rot=(0.57735,0.57735,0.57735;2.0944rad)
  Reference1 = -> Assembly [side_bearing_cilinders.Edge8,side_bearing_cilinders.Edge8]
  Reference2 = -> Assembly [spoon_holder_middle_section001.Face3,spoon_holder_middle_section001.Face3]
FEATURE [App::FeaturePython] Joint002  label="Fijo002"  # Assembly joint (typed FeaturePython)
  Activated = true
  AngleMax = 0
  AngleMin = 0
  Detach1 = false
  Detach2 = false
  Distance = 0
  Distance2 = 0
  EnableAngleMax = false
  EnableAngleMin = false
  EnableLengthMax = false
  EnableLengthMin = false
  JointType = 0 (Fixed)
  LengthMax = 0
  LengthMin = 0
  Placement1 = pos=(-46.8333,0,0) rot=(-0.707107,0,-0.707107;3.14159rad)
  Placement2 = pos=(46.8333,0,0) rot=(0.707107,0,0.707107;3.14159rad)
  Reference1 = -> Assembly [side_bearing_cilinders001.Edge1,side_bearing_cilinders001.Edge1]
  Reference2 = -> Assembly [side_bearing_cilinders.Face7,side_bearing_cilinders.Face7]
FEATURE [App::FeaturePython] Joint003  label="Fijo003"  # Assembly joint (typed FeaturePython)
  Activated = true
  AngleMax = 0
  AngleMin = 0
  Detach1 = false
  Detach2 = false
  Distance = 0
  Distance2 = 0
  EnableAngleMax = false
  EnableAngleMin = false
  EnableLengthMax = false
  EnableLengthMin = false
  JointType = 0 (Fixed)
  LengthMax = 0
  LengthMin = 0
  Placement1 = pos=(46.8333,0,0) rot=(-0.707107,0,-0.707107;3.14159rad)
  Placement2 = pos=(-2.84e-14,-60,45.77) rot=(0.57735,0.57735,0.57735;2.0944rad)
  Reference1 = -> Assembly [side_bearing_cilinders001.Edge8,side_bearing_cilinders001.Edge8]
  Reference2 = -> Assembly [spoon_holder_middle_section.Face18,spoon_holder_middle_section.Face18]
FEATURE [App::FeaturePython] Joint004  label="Fijo004"  # Assembly joint (typed FeaturePython)
  Activated = true
  AngleMax = 0
  AngleMin = 0
  Detach1 = false
  Detach2 = false
  Distance = 0
  Distance2 = 0
  EnableAngleMax = false
  EnableAngleMin = false
  EnableLengthMax = false
  EnableLengthMin = false
  JointType = 0 (Fixed)
  LengthMax = 0
  LengthMin = 0
  Placement1 = pos=(-46.8333,-7.1e-15,7.1e-15) rot=(-0.707107,0,-0.707107;3.14159rad)
  Placement2 = pos=(46.8333,0,0) rot=(-0.707107,0,-0.707107;3.14159rad)
  Reference1 = -> Assembly [side_bearing_cilinders002.Edge1,side_bearing_cilinders002.Edge1]
  Reference2 = -> Assembly [side_bearing_cilinders001.Face7,side_bearing_cilinders001.Face7]
FEATURE [App::FeaturePython] Joint005  label="Fijo005"  # Assembly joint (typed FeaturePython)
  Activated = true
  AngleMax = 0
  AngleMin = 0
  Detach1 = false
  Detach2 = false
  Distance = 0
  Distance2 = 0
  EnableAngleMax = false
  EnableAngleMin = false
  EnableLengthMax = false
  EnableLengthMin = false
  JointType = 0 (Fixed)
  LengthMax = 0
  LengthMin = 0
  Offset2 = pos=(0,0,0) rot=(0,0,1;3.14159rad)
  Placement1 = pos=(12,59.9992,45.7733) rot=(-0.57735,-0.57735,-0.57735;4.18879rad)
  Placement2 = pos=(38.8333,-7.1e-15,7.1e-15) rot=(0,1,0;1.5708rad)
  Reference1 = -> Assembly [spool_holder001.Face29,spool_holder001.Face29]
  Reference2 = -> Assembly [side_bearing_cilinders002.Face6,side_bearing_cilinders002.Edge1]
FEATURE [App::FeaturePython] Joint006  label="Fijo006"  # Assembly joint (typed FeaturePython)
  Activated = true
  AngleMax = 0
  AngleMin = 0
  Detach1 = false
  Detach2 = false
  Distance = 0
  Distance2 = 0
  EnableAngleMax = false
  EnableAngleMin = false
  EnableLengthMax = false
  EnableLengthMin = false
  JointType = 0 (Fixed)
  LengthMax = 0
  LengthMin = 0
  Placement1 = pos=(46.8333,0,0) rot=(-0.707107,0,-0.707107;3.14159rad)
  Placement2 = pos=(3.5,-60,45.7733) rot=(0.57735,0.57735,0.57735;2.0944rad)
  Reference1 = -> Assembly [side_bearing_cilinders005.Edge8,side_bearing_cilinders005.Edge8]
  Reference2 = -> Assembly [spool_holder001.Face15,spool_holder001.Face15]
FEATURE [App::FeaturePython] Joint007  label="Fijo007"  # Assembly joint (typed FeaturePython)
  Activated = true
  AngleMax = 0
  AngleMin = 0
  Detach1 = false
  Detach2 = false
  Distance = 0
  Distance2 = 0
  EnableAngleMax = false
  EnableAngleMin = false
  EnableLengthMax = false
  EnableLengthMin = false
  JointType = 0 (Fixed)
  LengthMax = 0
  LengthMin = 0
  Placement1 = pos=(-46.8333,0,0) rot=(-0.707107,0,-0.707107;3.14159rad)
  Placement2 = pos=(-1.42e-14,59.9999,45.77) rot=(0.57735,0.57735,0.57735;2.0944rad)
  Reference1 = -> Assembly [side_bearing_cilinders003.Edge1,side_bearing_cilinders003.Edge1]
  Reference2 = -> Assembly [spoon_holder_middle_section001.Face17,spoon_holder_middle_section001.Face17]
FEATURE [App::FeaturePython] Joint008  label="Fijo008"  # Assembly joint (typed FeaturePython)
  Activated = true
  AngleMax = 0
  AngleMin = 0
  Detach1 = false
  Detach2 = false
  Distance = 0
  Distance2 = 0
  EnableAngleMax = false
  EnableAngleMin = false
  EnableLengthMax = false
  EnableLengthMin = false
  JointType = 0 (Fixed)
  LengthMax = 0
  LengthMin = 0
  Placement1 = pos=(46.8333,-7.1e-15,0) rot=(0.707107,0,0.707107;3.14159rad)
  Placement2 = pos=(-46.8333,0,0) rot=(-0.707107,0,-0.707107;3.14159rad)
  Reference1 = -> Assembly [side_bearing_cilinders004.Edge8,side_bearing_cilinders004.Edge8]
  Reference2 = -> Assembly [side_bearing_cilinders003.Edge1,side_bearing_cilinders003.Edge1]
FEATURE [App::Link] spoon_holder_joins  label="spoon holder joins001"
  LinkPlacement = pos=(-1.0002,-60.0008,5.5) rot=(1,0,0;3.14159rad)
  LinkedObject = -> Body002
  Placement = pos=(-1.0002,-60.0008,5.5) rot=(1,0,0;3.14159rad)
FEATURE [App::Link] spoon_holder_joins001  label="spoon holder joins002"
  LinkPlacement = pos=(12,60,5.5) rot=(0,0,1;0rad)
  LinkedObject = -> Body002
  Placement = pos=(12,60,5.5) rot=(0,0,1;0rad)
FEATURE [App::Link] spoon_holder_joins002  label="spoon holder joins003"
  LinkPlacement = pos=(7,20.575,132.671) rot=(0,0,1;0rad)
  LinkedObject = -> Body002
  Placement = pos=(7,20.575,132.671) rot=(0,0,1;0rad)
FEATURE [App::Link] spoon_holder_joins003  label="spoon holder joins004"
  LinkPlacement = pos=(7,-20.575,132.671) rot=(0,0,1;0rad)
  LinkedObject = -> Body002
  Placement = pos=(7,-20.575,132.671) rot=(0,0,1;0rad)
FEATURE [App::FeaturePython] Joint009  label="Fijo009"  # Assembly joint (typed FeaturePython)
  Activated = true
  AngleMax = 0
  AngleMin = 0
  Detach1 = false
  Detach2 = false
  Distance = 0
  Distance2 = 0
  EnableAngleMax = false
  EnableAngleMin = false
  EnableLengthMax = false
  EnableLengthMin = false
  JointType = 0 (Fixed)
  LengthMax = 0
  LengthMin = 0
  Placement1 = pos=(7,20.575,132.671) rot=(0.57735,0.57735,0.57735;2.0944rad)
  Placement2 = pos=(0,0,0) rot=(0.57735,0.57735,0.57735;2.0944rad)
  Reference1 = -> Assembly [spool_holder.Edge96,spool_holder.Edge96]
  Reference2 = -> Assembly [spoon_holder_joins002.Edge2,spoon_holder_joins002.Edge2]
FEATURE [App::FeaturePython] Joint010  label="Fijo010"  # Assembly joint (typed FeaturePython)
  Activated = true
  AngleMax = 0
  AngleMin = 0
  Detach1 = false
  Detach2 = false
  Distance = 0
  Distance2 = 0
  EnableAngleMax = false
  EnableAngleMin = false
  EnableLengthMax = false
  EnableLengthMin = false
  JointType = 0 (Fixed)
  LengthMax = 0
  LengthMin = 0
  Placement1 = pos=(7,-20.575,132.671) rot=(0.707107,0,0.707107;3.14159rad)
  Placement2 = pos=(0,0,0) rot=(0.707107,0,0.707107;3.14159rad)
  Reference1 = -> Assembly [spool_holder.Face42,spool_holder.Edge1]
  Reference2 = -> Assembly [spoon_holder_joins003.Face2,spoon_holder_joins003.Face2]
FEATURE [App::FeaturePython] Joint011  label="Fijo011"  # Assembly joint (typed FeaturePython)
  Activated = true
  AngleMax = 0
  AngleMin = 0
  Detach1 = false
  Detach2 = false
  Distance = 0
  Distance2 = 0
  EnableAngleMax = false
  EnableAngleMin = false
  EnableLengthMax = false
  EnableLengthMin = false
  JointType = 0 (Fixed)
  LengthMax = 0
  LengthMin = 0
  Placement1 = pos=(0,0,0) rot=(0.57735,0.57735,0.57735;2.0944rad)
  Placement2 = pos=(12,60,5.5) rot=(0.57735,0.57735,0.57735;2.0944rad)
  Reference1 = -> Assembly [spoon_holder_joins001.Edge2,spoon_holder_joins001.Edge2]
  Reference2 = -> Assembly [spool_holder.Face28,spool_holder.Face28]
FEATURE [App::FeaturePython] Joint012  label="Fijo012"  # Assembly joint (typed FeaturePython)
  Activated = true
  AngleMax = 0
  AngleMin = 0
  Detach1 = false
  Detach2 = false
  Distance = 0
  Distance2 = 0
  EnableAngleMax = false
  EnableAngleMin = false
  EnableLengthMax = false
  EnableLengthMin = false
  JointType = 0 (Fixed)
  LengthMax = 0
  LengthMin = 0
  Placement1 = pos=(281,-6.39e-14,-1.981e-13) rot=(-0.57735,-0.57735,-0.57735;4.18879rad)
  Placement2 = pos=(12,60,5.5) rot=(-0.57735,-0.57735,-0.57735;4.18879rad)
  Reference1 = -> Assembly [spoon_holder_joins.Edge3,spoon_holder_joins.Edge3]
  Reference2 = -> Assembly [spool_holder001.Face28,spool_holder001.Face28]
FEATURE [Assembly::JointGroup] Joints
  Group = -> [GroundedJoint,Joint,Joint001,Joint002,Joint003,Joint004,Joint005,Joint006,Joint007,Joint008,Joint009,Joint010,Joint011,Joint012]
FEATURE [App::Link] spool_filament  label="spool filament001"
  LinkPlacement = pos=(55.0001,-3.05176e-05,147) rot=(0,0,1;0rad)
  LinkedObject = -> Body
  Placement = pos=(55.0001,-3.05176e-05,147) rot=(0,0,1;0rad)
FEATURE [App::Link] spool_filament001  label="spool filament002"
  LinkPlacement = pos=(239.967,-0.0337176,146.967) rot=(0,0,1;0rad)
  LinkedObject = -> Body
  Placement = pos=(239.967,-0.0337176,146.967) rot=(0,0,1;0rad)
FEATURE [App::Link] spool_filament002  label="spool filament003"
  LinkPlacement = pos=(147.933,-0.0672444,146.933) rot=(0,0,1;0rad)
  LinkedObject = -> Body
  Placement = pos=(147.933,-0.0672444,146.933) rot=(0,0,1;0rad)
FEATURE [Assembly::AssemblyObject] Assembly
  Group = -> [Joints,side_bearing_cilinders,side_bearing_cilinders001,side_bearing_cilinders002,side_bearing_cilinders003,side_bearing_cilinders004,side_bearing_cilinders005,spoon_holder_middle_section,spoon_holder_middle_section001,spool_holder,GroundedJoint,spool_holder001,Joint,Joint001,Joint002,Joint003,Joint004,Joint005,Joint006,Joint007,Joint008,spoon_holder_joins,spoon_holder_joins001,+9 more]
  Origin = -> Origin008
  Type = Assembly
